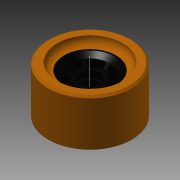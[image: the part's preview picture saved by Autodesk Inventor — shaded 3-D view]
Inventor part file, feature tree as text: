
AUTODESK INVENTOR PART (.ipt)
format: ipt  version: 2014 SP1 (Build 180222100, 222)  size: 380,416 bytes
history: native  units: in
note: dims shown in document units (in); Inventor stores cm internally (conversion verified against a paired STEP export)
features: extrude x4, chamfer x4, sketch x3, fillet x3, pattern_circular x2, revolve x1
ambient origin geometry x8: Origin, YZ Plane, XZ Plane, XY Plane, X Axis, Y Axis, Z Axis, Center Point
bodies: Solid1 (feature_tree)
feature tree (17):
  revolve  "Revolution1"  [1 undecoded]
  sketch  "Sketch3"  dims[d4=0.44in d6=0.815in]
  extrude  "Bearing Holder"  Depth=0.815in
  extrude  "Bearing Holder Lip"  Depth=0.02in
  extrude  "Spoke"  Depth=0.02in
  chamfer  "Chamfer1"  Distance=0.36in
  chamfer  "Chamfer2"  Angle=90.0deg  [1 undecoded]
  fillet  "Fillet1"  Radius=1.14in
  pattern_circular  "Spoke Pattern"  [2 undecoded]
  extrude  "Nib"  Depth=0.02in
  fillet  "Fillet2"  Radius=0.1in
  fillet  "Fillet3"  Radius=0.296in
  pattern_circular  "Nib Pattern"  [2 undecoded]
  chamfer  "Wheel Inner Chamfer"  Distance=0.296in
  chamfer  "Wheel Outer Chamfer"  Distance=0.168in Angle=45.0deg
  sketch  "Sketch2"  dims[d0=1.7717in d2=0.38in]
  sketch  "Sketch5"  dims[d7=0.29in d9=1.025in d10=0.2898in d11=0.36in d12=90.0deg d13=1.14in d14=0.834in d15=0.0in d17=0.865in d18=0.1in d19=0.296in d20=0.0in d21=0.15in d22=0.296in d23=0.0in d24=0.168in d25=0.18in d26=45.0deg d27=0.05in d28=2.3622in d29=360.0deg d31=0.168in d32=0.18in d33=45.0deg d34=30.0deg d35=0.09in d36=0.06in d37=0.296in d38=0.0in d39=0.05in d40=0.02in d41=2.3622in d42=360.0deg d44=0.08in d45=0.18in d46=45.0deg d47=0.08in d48=0.292in d49=45.0deg]
note: 6 required parameter values undecoded (feature->parameter linkage not recoverable at this tier; creation-order binding heuristic only, values carry confidence <= 0.55)